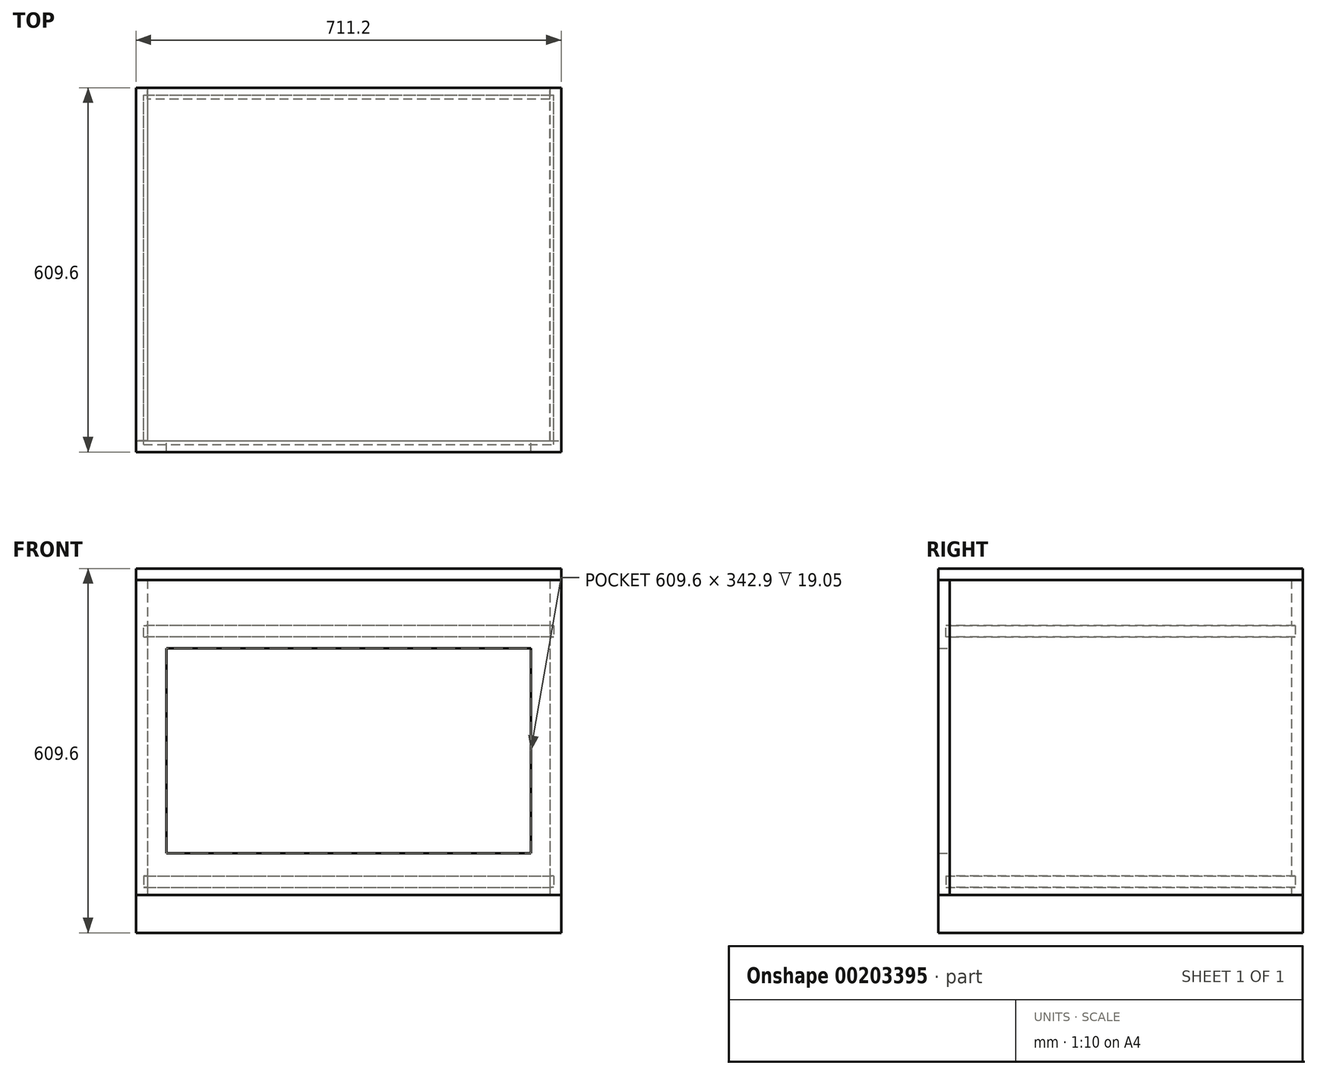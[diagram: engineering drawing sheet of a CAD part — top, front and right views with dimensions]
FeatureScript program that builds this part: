
annotation { "Feature Type Name" : "Feature", "Feature Type Description" : "" }
export const myFeature = defineFeature(function(context is Context, id is Id, definition is map)
    precondition{}
    {
        {
            var Q0;
            Q0=qCreatedBy(makeId("Top.planeOp"),FACE);
            var sketch = newSketch(context, id + "F0", { "sketchPlane" : qUnion([Q0])});
            skLineSegment(sketch, "E0.bottom", {"start": v(355.6, 304.8) * mm, "end": v(-355.6, 304.8) * mm});
            skLineSegment(sketch, "E0.top", {"start": v(355.6, -304.8) * mm, "end": v(-355.6, -304.8) * mm});
            skLineSegment(sketch, "E0.left", {"start": v(355.6, 304.8) * mm, "end": v(355.6, -304.8) * mm});
            skLineSegment(sketch, "E0.right", {"start": v(-355.6, 304.8) * mm, "end": v(-355.6, -304.8) * mm});
            skPoint(sketch, "E0.middle", {"position": v(0, 0) * mm});
            skSolve(sketch);
        }
        {
            var Q0;
            Q0=makeQuery(id+"F0.imprint","IMPRINT",FACE,{"disambiguationData":[TD([[makeQuery(id+"F0.imprint","IMPRINT",EDGE,{"derivedFrom":sQuery(id+"F0.wireOp",EDGE,"E0.bottom")}),1.0]])]});
            extrude(context, id + "F1", {"entities" : qUnion([Q0]), "depth" : 609.6 * mm});
        }
        {
            var Q0;
            Q0=makeQuery(id+"F1.opExtrude","CAP_FACE",FACE,{"disambiguationData":[OSD([sQuery(id+"F0.wireOp",EDGE,"E0.bottom"),sQuery(id+"F0.wireOp",EDGE,"E0.top"),sQuery(id+"F0.wireOp",EDGE,"E0.left"),sQuery(id+"F0.wireOp",EDGE,"E0.right")])],"isStart":false});
            var sketch = newSketch(context, id + "F2", { "sketchPlane" : qUnion([Q0])});
            skSolve(sketch);
        }
        {
            var Q0;
            Q0=makeQuery(id+"F2.imprint","IMPRINT",FACE,{"disambiguationData":[TD([[makeQuery(id+"F2.imprint","IMPRINT",EDGE,{"derivedFrom":makeQuery(id+"F1.opExtrude","CAP_EDGE",EDGE,{"disambiguationData":[OSD([sQuery(id+"F0.wireOp",EDGE,"E0.bottom")])],"isStart":false})}),1.0]])]});
            extrude(context, id + "F3", {"entities" : qUnion([Q0]), "oppositeDirection" : true, "depth" : 19.05 * mm});
        }
        {
            var Q0;
            Q0=makeQuery(id+"F1.opExtrude","SWEPT_FACE",FACE,{"disambiguationData":[OSD([sQuery(id+"F0.wireOp",EDGE,"E0.left")])]});
            var sketch = newSketch(context, id + "F4", { "sketchPlane" : qUnion([Q0])});
            skLineSegment(sketch, "E1.0", {"start": v(304.8, 590.55) * mm, "end": v(-304.8, 590.55) * mm});
            skLineSegment(sketch, "E2", {"start": v(-285.75, 590.55) * mm, "end": v(-285.75, 63.5) * mm});
            skLineSegment(sketch, "E3", {"start": v(-285.75, 63.5) * mm, "end": v(304.8, 63.5) * mm});
            skSolve(sketch);
        }
        {
            var Q0;
            {var subQ0=sQuery(id+"F4.wireOp",EDGE,"E1.0");Q0=makeQuery(id+"F4.imprint","IMPRINT",FACE,{"disambiguationData":[TD([[makeQuery(id+"F4.imprint","IMPRINT",EDGE,{"derivedFrom":subQ0}),1.0]])]});}
            extrude(context, id + "F5", {"entities" : qUnion([Q0]), "oppositeDirection" : true, "depth" : 19.05 * mm});
        }
        {
            var Q0;
            Q0=makeQuery(id+"F5.opExtrude","SWEPT_BODY",BODY,{"disambiguationData":[OSD([sQuery(id+"F0.wireOp",EDGE,"E0.bottom"),sQuery(id+"F0.wireOp",EDGE,"E0.top"),sQuery(id+"F0.wireOp",EDGE,"E0.left"),sQuery(id+"F4.wireOp",EDGE,"E1.0")])]});
            var Q1;
            Q1=qCreatedBy(makeId("Right.planeOp"),FACE);
            mirror(context, id + "F6", {"entities" : qUnion([Q0]), "mirrorPlane" : qUnion([Q1])});
        }
        {
            var Q0;
            Q0=makeQuery(id+"F1.opExtrude","SWEPT_FACE",FACE,{"disambiguationData":[OSD([sQuery(id+"F0.wireOp",EDGE,"E0.top")])]});
            var sketch = newSketch(context, id + "F7", { "sketchPlane" : qUnion([Q0])});
            skLineSegment(sketch, "E4.0", {"start": v(355.6, 590.55) * mm, "end": v(-355.6, 590.55) * mm});
            skLineSegment(sketch, "E5.0", {"start": v(355.6, 590.55) * mm, "end": v(355.6, 63.5) * mm});
            skLineSegment(sketch, "E5.1", {"start": v(-355.6, 590.55) * mm, "end": v(-355.6, 63.5) * mm});
            skLineSegment(sketch, "E6", {"start": v(-355.6, 63.5) * mm, "end": v(355.6, 63.5) * mm});
            skSolve(sketch);
        }
        {
            var Q0;
            Q0=makeQuery(id+"F7.imprint","IMPRINT",FACE,{"disambiguationData":[TD([[makeQuery(id+"F7.imprint","IMPRINT",EDGE,{"derivedFrom":sQuery(id+"F7.wireOp",EDGE,"E4.0")}),1.0]])]});
            extrude(context, id + "F8", {"entities" : qUnion([Q0]), "oppositeDirection" : true, "depth" : 19.05 * mm});
        }
        {
            var Q0;
            Q0=makeQuery(id+"F1.opExtrude","SWEPT_FACE",FACE,{"disambiguationData":[OSD([sQuery(id+"F0.wireOp",EDGE,"E0.bottom")])]});
            var sketch = newSketch(context, id + "F9", { "sketchPlane" : qUnion([Q0])});
            skLineSegment(sketch, "E7.0", {"start": v(-336.55, 590.55) * mm, "end": v(-336.55, 63.5) * mm});
            skLineSegment(sketch, "E7.1", {"start": v(-355.6, 590.55) * mm, "end": v(355.6, 590.55) * mm});
            skLineSegment(sketch, "E7.2", {"start": v(336.55, 590.55) * mm, "end": v(336.55, 63.5) * mm});
            skLineSegment(sketch, "E8", {"start": v(-336.55, 63.5) * mm, "end": v(336.55, 63.5) * mm});
            skSolve(sketch);
        }
        {
            var Q0;
            {var subQ0=sQuery(id+"F9.wireOp",EDGE,"E7.0");Q0=makeQuery(id+"F9.imprint","IMPRINT",FACE,{"disambiguationData":[TD([[makeQuery(id+"F9.imprint","IMPRINT",EDGE,{"derivedFrom":subQ0}),1.0]])]});}
            extrude(context, id + "F10", {"entities" : qUnion([Q0]), "oppositeDirection" : true, "depth" : 19.05 * mm});
        }
        {
            var Q0;
            Q0=qCreatedBy(makeId("Top.planeOp"),FACE);
            cPlane(context, id + "F11", {"entities" : qUnion([Q0]), "cplaneType" : CPlaneType.OFFSET, "offset" : 76.2 * mm, "width" : 152.4 * mm, "height" : 152.4 * mm});
        }
        {
            var Q0;
            Q0=qCreatedBy(id+"F11.planeOp",FACE);
            var sketch = newSketch(context, id + "F12", { "sketchPlane" : qUnion([Q0])});
            skLineSegment(sketch, "E9.0", {"start": v(-336.55, -285.75) * mm, "end": v(336.55, -285.75) * mm});
            skLineSegment(sketch, "E9.1", {"start": v(336.55, -285.75) * mm, "end": v(336.55, 285.75) * mm});
            skLineSegment(sketch, "E9.2", {"start": v(-336.55, -285.75) * mm, "end": v(-336.55, 285.75) * mm});
            skLineSegment(sketch, "E9.3", {"start": v(336.55, 285.75) * mm, "end": v(-336.55, 285.75) * mm});
            skPoint(sketch, "E10.orphan", {"position": v(-355.6, -285.75) * mm});
            skPoint(sketch, "E11.orphan", {"position": v(-336.55, 304.8) * mm});
            skPoint(sketch, "E12.orphan", {"position": v(336.55, 304.8) * mm});
            skPoint(sketch, "E13.orphan", {"position": v(355.6, -285.75) * mm});
            skLineSegment(sketch, "E14.0", {"start": v(-342.9, -292.1) * mm, "end": v(342.9, -292.1) * mm});
            skLineSegment(sketch, "E14.1", {"start": v(-342.9, -292.1) * mm, "end": v(-342.9, 292.1) * mm});
            skLineSegment(sketch, "E14.2", {"start": v(342.9, 292.1) * mm, "end": v(-342.9, 292.1) * mm});
            skLineSegment(sketch, "E14.3", {"start": v(342.9, -292.1) * mm, "end": v(342.9, 292.1) * mm});
            skSolve(sketch);
        }
        {
            var Q0;
            Q0=makeQuery(id+"F12.imprint","IMPRINT",FACE,{"disambiguationData":[TD([[makeQuery(id+"F12.imprint","IMPRINT",EDGE,{"derivedFrom":sQuery(id+"F12.wireOp",EDGE,"E9.0")}),-1.0]])]});
            var Q1;
            Q1=makeQuery(id+"F12.imprint","IMPRINT",FACE,{"disambiguationData":[TD([[makeQuery(id+"F12.imprint","IMPRINT",EDGE,{"derivedFrom":sQuery(id+"F12.wireOp",EDGE,"E9.0")}),1.0]])]});
            extrude(context, id + "F13", {"entities" : qUnion([Q0, Q1]), "depth" : 19.05 * mm});
        }
        {
            var Q0;
            Q0=makeQuery(id+"F3.opExtrude","CAP_FACE",FACE,{"disambiguationData":[OSD([sQuery(id+"F0.wireOp",EDGE,"E0.bottom"),sQuery(id+"F0.wireOp",EDGE,"E0.top"),sQuery(id+"F0.wireOp",EDGE,"E0.left"),sQuery(id+"F0.wireOp",EDGE,"E0.right")])],"isStart":false});
            cPlane(context, id + "F14", {"entities" : qUnion([Q0]), "cplaneType" : CPlaneType.OFFSET, "offset" : 76.2 * mm, "width" : 152.4 * mm, "height" : 152.4 * mm});
        }
        {
            var Q0;
            Q0=qCreatedBy(id+"F14.planeOp",FACE);
            var sketch = newSketch(context, id + "F15", { "sketchPlane" : qUnion([Q0])});
            skLineSegment(sketch, "E15.0.0", {"start": v(355.6, 304.8) * mm, "end": v(-355.6, 304.8) * mm});
            skLineSegment(sketch, "E15.0.1", {"start": v(-355.6, 304.8) * mm, "end": v(-355.6, -304.8) * mm});
            skLineSegment(sketch, "E15.0.2", {"start": v(-355.6, -304.8) * mm, "end": v(355.6, -304.8) * mm});
            skLineSegment(sketch, "E15.0.3", {"start": v(355.6, -304.8) * mm, "end": v(355.6, 304.8) * mm});
            skLineSegment(sketch, "E16.0", {"start": v(342.9, 292.1) * mm, "end": v(-342.9, 292.1) * mm});
            skLineSegment(sketch, "E16.1", {"start": v(342.9, -292.1) * mm, "end": v(342.9, 292.1) * mm});
            skLineSegment(sketch, "E16.2", {"start": v(-342.9, -292.1) * mm, "end": v(342.9, -292.1) * mm});
            skLineSegment(sketch, "E16.3", {"start": v(-342.9, 292.1) * mm, "end": v(-342.9, -292.1) * mm});
            skSolve(sketch);
        }
        {
            var Q0;
            Q0=makeQuery(id+"F15.imprint","IMPRINT",FACE,{"disambiguationData":[TD([[makeQuery(id+"F15.imprint","IMPRINT",EDGE,{"derivedFrom":sQuery(id+"F15.wireOp",EDGE,"E16.0")}),1.0]])]});
            extrude(context, id + "F16", {"entities" : qUnion([Q0]), "depth" : 19.05 * mm});
        }
        {
            var Q0;
            Q0=makeQuery(id+"F8.opExtrude","CAP_FACE",FACE,{"disambiguationData":[OSD([sQuery(id+"F7.wireOp",EDGE,"E4.0"),sQuery(id+"F7.wireOp",EDGE,"E5.0"),sQuery(id+"F7.wireOp",EDGE,"E5.1"),sQuery(id+"F7.wireOp",EDGE,"E6")])],"isStart":false});
            var sketch = newSketch(context, id + "F17", { "sketchPlane" : qUnion([Q0])});
            skLineSegment(sketch, "E17.0", {"start": v(-342.9, 495.3) * mm, "end": v(342.9, 495.3) * mm});
            skLineSegment(sketch, "E18.0", {"start": v(-336.55, 590.55) * mm, "end": v(-336.55, 63.5) * mm});
            skLineSegment(sketch, "E19.0", {"start": v(342.9, 95.25) * mm, "end": v(-342.9, 95.25) * mm});
            skLineSegment(sketch, "E20.0", {"start": v(336.55, 590.55) * mm, "end": v(336.55, 63.5) * mm});
            skLineSegment(sketch, "E21.bottom", {"start": v(304.8, 133.35) * mm, "end": v(-304.8, 133.35) * mm});
            skLineSegment(sketch, "E21.top", {"start": v(304.8, 476.25) * mm, "end": v(-304.8, 476.25) * mm});
            skLineSegment(sketch, "E21.left", {"start": v(304.8, 133.35) * mm, "end": v(304.8, 476.25) * mm});
            skLineSegment(sketch, "E21.right", {"start": v(-304.8, 133.35) * mm, "end": v(-304.8, 476.25) * mm});
            skSolve(sketch);
        }
        {
            var Q0;
            Q0=makeQuery(id+"F17.imprint","IMPRINT",FACE,{"disambiguationData":[TD([[makeQuery(id+"F17.imprint","IMPRINT",EDGE,{"derivedFrom":sQuery(id+"F17.wireOp",EDGE,"E21.bottom")}),-1.0]])]});
            extrude(context, id + "F18", {"entities" : qUnion([Q0]), "operationType" : NewBodyOperationType.REMOVE, "endBound" : BoundingType.UP_TO_NEXT, "oppositeDirection" : true, "depth" : 25.4 * mm});
        }
        {
            var Q0;
            Q0=makeQuery(id+"F13.opExtrude","SWEPT_BODY",BODY,{"disambiguationData":[OSD([sQuery(id+"F12.wireOp",EDGE,"E14.0"),sQuery(id+"F12.wireOp",EDGE,"E14.1"),sQuery(id+"F12.wireOp",EDGE,"E14.2"),sQuery(id+"F12.wireOp",EDGE,"E14.3")])]});
            var Q1;
            Q1=makeQuery(id+"F10.opExtrude","SWEPT_BODY",BODY,{"disambiguationData":[OSD([sQuery(id+"F9.wireOp",EDGE,"E7.0"),sQuery(id+"F9.wireOp",EDGE,"E7.1"),sQuery(id+"F9.wireOp",EDGE,"E7.2"),sQuery(id+"F9.wireOp",EDGE,"E8")])]});
            var Q2;
            Q2=makeQuery(id+"F6.opPattern","COPY",BODY,{"derivedFrom":makeQuery(id+"F5.opExtrude","SWEPT_BODY",BODY,{"disambiguationData":[OSD([sQuery(id+"F0.wireOp",EDGE,"E0.bottom"),sQuery(id+"F0.wireOp",EDGE,"E0.left"),sQuery(id+"F4.wireOp",EDGE,"E1.0"),sQuery(id+"F4.wireOp",EDGE,"E2"),sQuery(id+"F4.wireOp",EDGE,"E3")])]}),"instanceName":"1"});
            var Q3;
            Q3=makeQuery(id+"F8.opExtrude","SWEPT_BODY",BODY,{"disambiguationData":[OSD([sQuery(id+"F7.wireOp",EDGE,"E4.0"),sQuery(id+"F7.wireOp",EDGE,"E5.0"),sQuery(id+"F7.wireOp",EDGE,"E5.1"),sQuery(id+"F7.wireOp",EDGE,"E6")])]});
            var Q4;
            Q4=makeQuery(id+"F5.opExtrude","SWEPT_BODY",BODY,{"disambiguationData":[OSD([sQuery(id+"F0.wireOp",EDGE,"E0.bottom"),sQuery(id+"F0.wireOp",EDGE,"E0.left"),sQuery(id+"F4.wireOp",EDGE,"E1.0"),sQuery(id+"F4.wireOp",EDGE,"E2"),sQuery(id+"F4.wireOp",EDGE,"E3")])]});
            booleanBodies(context, id + "F19", {"operationType" : BooleanOperationType.SUBTRACTION, "tools" : qUnion([Q0]), "targets" : qUnion([Q1, Q2, Q3, Q4]), "keepTools" : true});
        }
        {
            var Q0;
            Q0=makeQuery(id+"F16.opExtrude","SWEPT_BODY",BODY,{"disambiguationData":[OSD([sQuery(id+"F15.wireOp",EDGE,"E16.0"),sQuery(id+"F15.wireOp",EDGE,"E16.1"),sQuery(id+"F15.wireOp",EDGE,"E16.2"),sQuery(id+"F15.wireOp",EDGE,"E16.3")])]});
            var Q1;
            Q1=makeQuery(id+"F8.opExtrude","SWEPT_BODY",BODY,{"disambiguationData":[OSD([sQuery(id+"F7.wireOp",EDGE,"E4.0"),sQuery(id+"F7.wireOp",EDGE,"E5.0"),sQuery(id+"F7.wireOp",EDGE,"E5.1"),sQuery(id+"F7.wireOp",EDGE,"E6")])]});
            var Q2;
            Q2=makeQuery(id+"F6.opPattern","COPY",BODY,{"derivedFrom":makeQuery(id+"F5.opExtrude","SWEPT_BODY",BODY,{"disambiguationData":[OSD([sQuery(id+"F0.wireOp",EDGE,"E0.bottom"),sQuery(id+"F0.wireOp",EDGE,"E0.left"),sQuery(id+"F4.wireOp",EDGE,"E1.0"),sQuery(id+"F4.wireOp",EDGE,"E2"),sQuery(id+"F4.wireOp",EDGE,"E3")])]}),"instanceName":"1"});
            var Q3;
            Q3=makeQuery(id+"F10.opExtrude","SWEPT_BODY",BODY,{"disambiguationData":[OSD([sQuery(id+"F9.wireOp",EDGE,"E7.0"),sQuery(id+"F9.wireOp",EDGE,"E7.1"),sQuery(id+"F9.wireOp",EDGE,"E7.2"),sQuery(id+"F9.wireOp",EDGE,"E8")])]});
            var Q4;
            Q4=makeQuery(id+"F5.opExtrude","SWEPT_BODY",BODY,{"disambiguationData":[OSD([sQuery(id+"F0.wireOp",EDGE,"E0.bottom"),sQuery(id+"F0.wireOp",EDGE,"E0.left"),sQuery(id+"F4.wireOp",EDGE,"E1.0"),sQuery(id+"F4.wireOp",EDGE,"E2"),sQuery(id+"F4.wireOp",EDGE,"E3")])]});
            booleanBodies(context, id + "F20", {"operationType" : BooleanOperationType.SUBTRACTION, "tools" : qUnion([Q0]), "targets" : qUnion([Q1, Q2, Q3, Q4]), "keepTools" : true});
        }
    });
